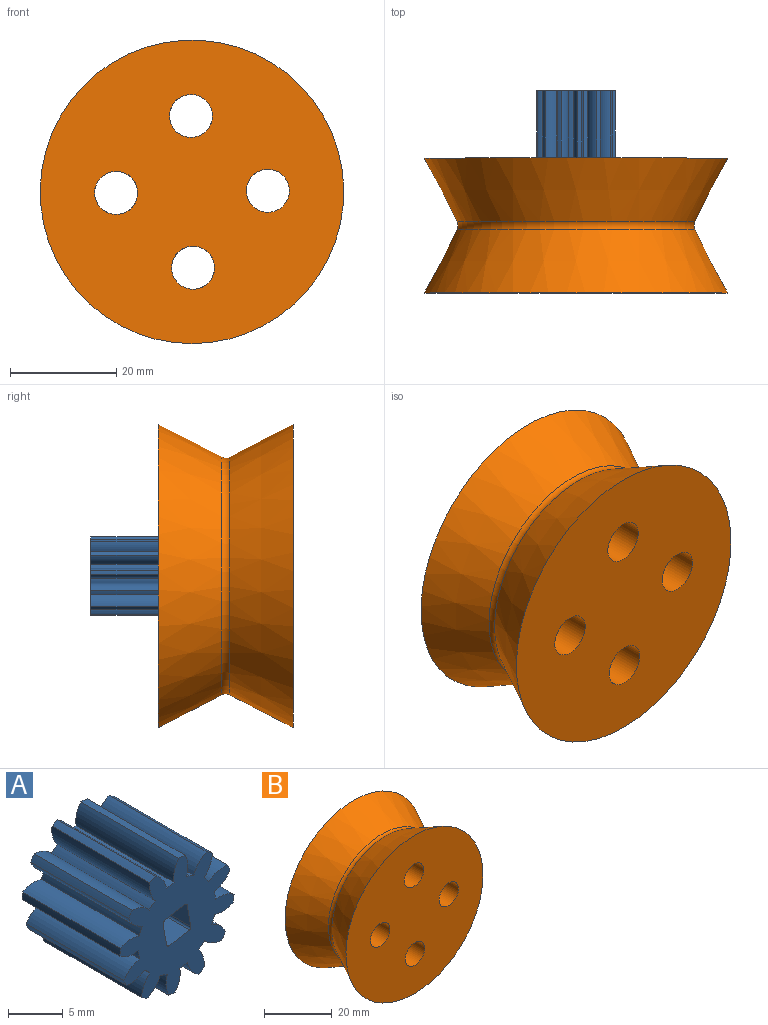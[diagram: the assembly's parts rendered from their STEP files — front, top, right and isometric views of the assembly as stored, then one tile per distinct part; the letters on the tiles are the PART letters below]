
ASSEMBLY  parts=2 mates=1
PART A: 58 faces, bbox 14.8x12.7x14.8 mm
  f0: cylinder r=0.25mm len=12.7mm, axis (0,-1,0), area 5.1mm2, adj f49,f50,f54,f55
  f1: cylinder r=3mm len=12.7mm, axis (0,-1,0), area 32.3mm2, adj f32,f33,f49,f50
  f2: cylinder r=3mm len=12.7mm, axis (0,-1,0), area 32.3mm2, adj f29,f30,f49,f50
  f3: cylinder r=3mm len=12.7mm, axis (0,-1,0), area 32.3mm2, adj f12,f13,f49,f50
  f4: cylinder r=7.4mm len=12.7mm, axis (0,-1,0), area 10.5mm2, adj f5,f48,f49,f50
  f5: cylinder r=3mm len=12.7mm, axis (0,-1,0), area 32.3mm2, adj f4,f6,f49,f50
  f6: cylinder r=5.03mm len=12.7mm, axis (0,-1,0), area 12.7mm2, adj f5,f7,f49,f50
  f7: cylinder r=3mm len=12.7mm, axis (0,-1,0), area 32.3mm2, adj f6,f8,f49,f50
  f8: cylinder r=7.4mm len=12.7mm, axis (0,-1,0), area 10.5mm2, adj f7,f9,f49,f50
  f9: cylinder r=3mm len=12.7mm, axis (0,-1,0), area 32.3mm2, adj f8,f10,f49,f50
  f10: cylinder r=5.03mm len=12.7mm, axis (0,-1,0), area 12.7mm2, adj f9,f11,f49,f50
  f11: cylinder r=3mm len=12.7mm, axis (0,-1,0), area 32.3mm2, adj f10,f12,f49,f50
  f12: cylinder r=7.4mm len=12.7mm, axis (0,-1,0), area 10.5mm2, adj f3,f11,f49,f50
  f13: cylinder r=5.03mm len=12.7mm, axis (0,-1,0), area 12.7mm2, adj f3,f14,f49,f50
  f14: cylinder r=3mm len=12.7mm, axis (0,-1,0), area 32.3mm2, adj f13,f15,f49,f50
  f15: cylinder r=7.4mm len=12.7mm, axis (0,-1,0), area 10.5mm2, adj f14,f16,f49,f50
  f16: cylinder r=3mm len=12.7mm, axis (0,-1,0), area 32.3mm2, adj f15,f17,f49,f50
  f17: cylinder r=5.03mm len=12.7mm, axis (0,-1,0), area 12.7mm2, adj f16,f18,f49,f50
  f18: cylinder r=3mm len=12.7mm, axis (0,-1,0), area 32.3mm2, adj f17,f19,f49,f50
  f19: cylinder r=7.4mm len=12.7mm, axis (0,-1,0), area 10.5mm2, adj f18,f20,f49,f50
  f20: cylinder r=3mm len=12.7mm, axis (0,-1,0), area 32.3mm2, adj f19,f21,f49,f50
  f21: cylinder r=5.03mm len=12.7mm, axis (0,-1,0), area 12.7mm2, adj f20,f22,f49,f50
  f22: cylinder r=3mm len=12.7mm, axis (0,-1,0), area 32.3mm2, adj f21,f23,f49,f50
  f23: cylinder r=7.4mm len=12.7mm, axis (0,-1,0), area 10.5mm2, adj f22,f24,f49,f50
  f24: cylinder r=3mm len=12.7mm, axis (0,-1,0), area 32.3mm2, adj f23,f25,f49,f50
  f25: cylinder r=5.03mm len=12.7mm, axis (0,-1,0), area 12.7mm2, adj f24,f26,f49,f50
  f26: cylinder r=3mm len=12.7mm, axis (0,-1,0), area 32.3mm2, adj f25,f27,f49,f50
  f27: cylinder r=7.4mm len=12.7mm, axis (0,-1,0), area 10.5mm2, adj f26,f28,f49,f50
  f28: cylinder r=3mm len=12.7mm, axis (0,-1,0), area 32.3mm2, adj f27,f29,f49,f50
  f29: cylinder r=5.03mm len=12.7mm, axis (0,-1,0), area 12.7mm2, adj f2,f28,f49,f50
  f30: cylinder r=7.4mm len=12.7mm, axis (0,-1,0), area 10.5mm2, adj f2,f31,f49,f50
  f31: cylinder r=3mm len=12.7mm, axis (0,-1,0), area 32.3mm2, adj f30,f32,f49,f50
  f32: cylinder r=5.03mm len=12.7mm, axis (0,-1,0), area 12.7mm2, adj f1,f31,f49,f50
  f33: cylinder r=7.4mm len=12.7mm, axis (0,-1,0), area 10.5mm2, adj f1,f34,f49,f50
  f34: cylinder r=3mm len=12.7mm, axis (0,-1,0), area 32.3mm2, adj f33,f35,f49,f50
  f35: cylinder r=5.03mm len=12.7mm, axis (0,-1,0), area 12.7mm2, adj f34,f36,f49,f50
  f36: cylinder r=3mm len=12.7mm, axis (0,-1,0), area 32.3mm2, adj f35,f37,f49,f50
  f37: cylinder r=7.4mm len=12.7mm, axis (0,-1,0), area 10.5mm2, adj f36,f38,f49,f50
  f38: cylinder r=3mm len=12.7mm, axis (0,-1,0), area 32.3mm2, adj f37,f39,f49,f50
  f39: cylinder r=5.03mm len=12.7mm, axis (0,-1,0), area 12.7mm2, adj f38,f40,f49,f50
  f40: cylinder r=3mm len=12.7mm, axis (0,-1,0), area 32.3mm2, adj f39,f41,f49,f50
  f41: cylinder r=7.4mm len=12.7mm, axis (0,-1,0), area 10.5mm2, adj f40,f42,f49,f50
  f42: cylinder r=3mm len=12.7mm, axis (0,-1,0), area 32.3mm2, adj f41,f43,f49,f50
  f43: cylinder r=5.03mm len=12.7mm, axis (0,-1,0), area 12.7mm2, adj f42,f44,f49,f50
  f44: cylinder r=3mm len=12.7mm, axis (0,-1,0), area 32.3mm2, adj f43,f45,f49,f50
  f45: cylinder r=7.4mm len=12.7mm, axis (0,-1,0), area 10.5mm2, adj f44,f46,f49,f50
  f46: cylinder r=3mm len=12.7mm, axis (0,-1,0), area 32.3mm2, adj f45,f47,f49,f50
  f47: cylinder r=5.03mm len=12.7mm, axis (0,-1,0), area 12.7mm2, adj f46,f48,f49,f50
  f48: cylinder r=3mm len=12.7mm, axis (0,-1,0), area 32.3mm2, adj f4,f47,f49,f50
  f49: plane 14.8x14.8mm, normal (0,1,0), area 114.9mm2, adj f0,f1,f2,f3,f4,f5,f6,f7
  f50: plane 14.8x14.8mm, normal (0,-1,0), area 114.9mm2, adj f0,f1,f2,f3,f4,f5,f6,f7
  f51: cylinder r=0.25mm len=12.7mm, axis (0,-1,0), area 5.1mm2, adj f49,f50,f52,f57
  f52: plane 12.7x2.63mm, normal (-0.98,0,-0.17), area 33.9mm2, adj f49,f50,f51,f53
  f53: cylinder r=0.25mm len=12.7mm, axis (0,-1,0), area 5.1mm2, adj f49,f50,f52,f54
  f54: plane 12.7x2.63mm, normal (-0.17,0,0.98), area 33.9mm2, adj f0,f49,f50,f53
  f55: plane 12.7x2.63mm, normal (0.98,0,0.17), area 33.9mm2, adj f0,f49,f50,f56
  f56: cylinder r=0.25mm len=12.7mm, axis (0,-1,0), area 5.1mm2, adj f49,f50,f55,f57
  f57: plane 12.7x2.63mm, normal (0.17,0,-0.98), area 33.9mm2, adj f49,f50,f51,f56
PART B: 9 faces, bbox 57.2x25.4x57.2 mm
  f0: cone r=22.41mm half-angle=27.3deg, axis (0,-1,0), area 2152.8mm2, adj f1,f4
  f1: plane 57.15x57.15mm, normal (0,-1,0), area 2359.3mm2, adj f0,f5,f6,f7,f8
  f2: plane 57.15x57.15mm, normal (0,1,0), area 2359.3mm2, adj f3,f5,f6,f7,f8
  f3: cone r=22.41mm half-angle=27.3deg, axis (0,1,0), area 2152.8mm2, adj f2,f4
  f4: torus R=23.88mm, axis (0,-1,0), area 220.4mm2, adj f0,f3
  f5: cylinder r=4.05mm len=25.4mm, axis (0,-1,0), area 646.1mm2, adj f1,f2
  f6: cylinder r=4.05mm len=25.4mm, axis (0,-1,0), area 646.1mm2, adj f1,f2
  f7: cylinder r=4.05mm len=25.4mm, axis (0,-1,0), area 646.1mm2, adj f1,f2
  f8: cylinder r=4.05mm len=25.4mm, axis (0,-1,0), area 646.1mm2, adj f1,f2
PLACE A t=(-183.33,35.26,192.61)mm
PLACE B t=(-183.33,16.21,192.61)mm
MATE fastened A.f4 <-> B.f3  axis (0,-1,0) through (-183.33,28.91,192.61)mm
